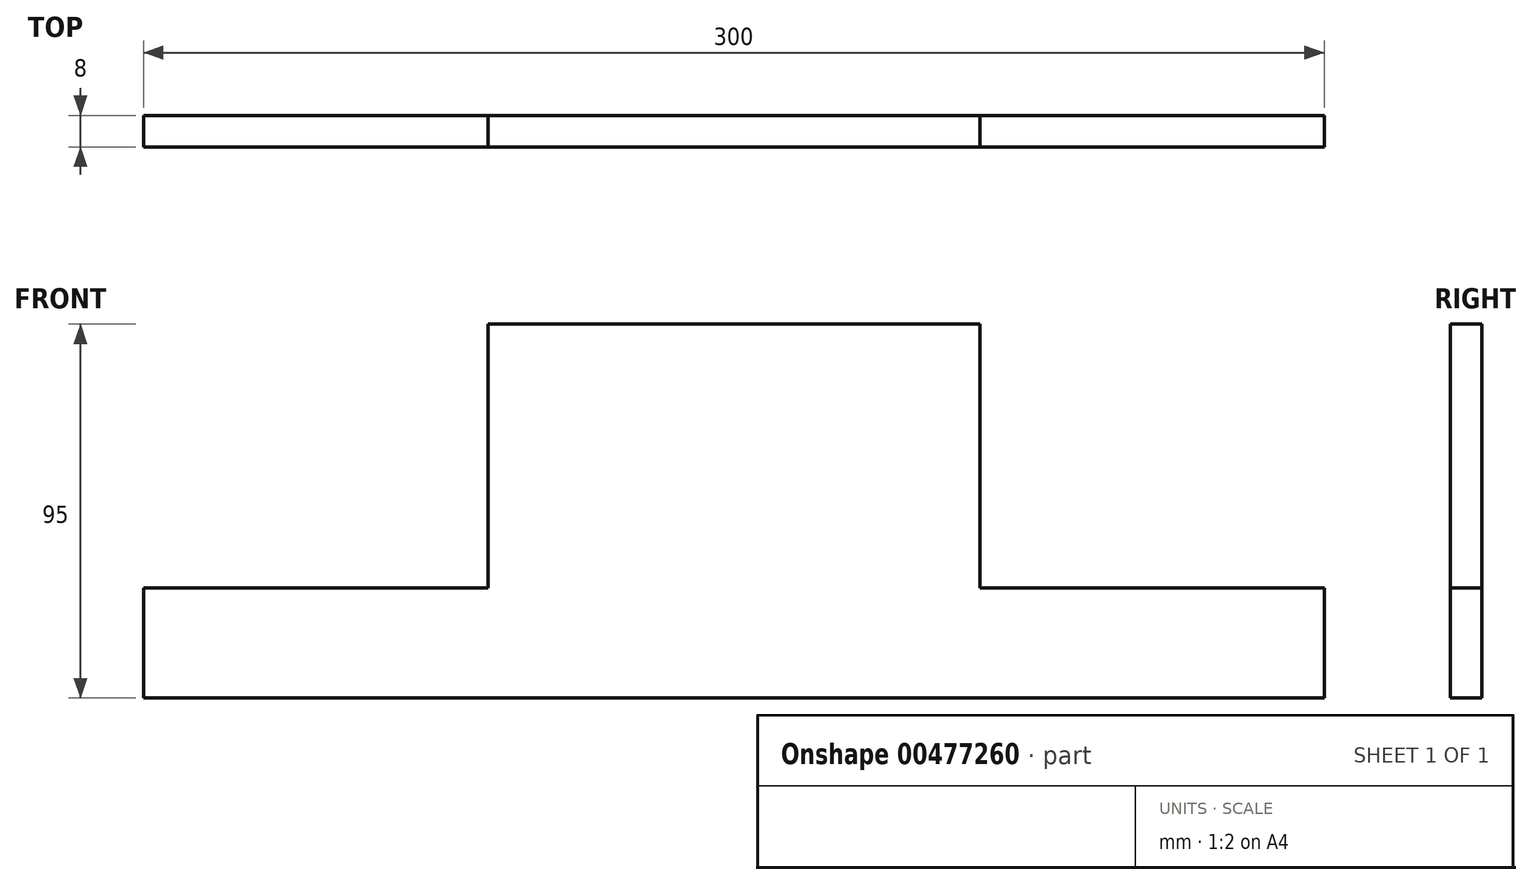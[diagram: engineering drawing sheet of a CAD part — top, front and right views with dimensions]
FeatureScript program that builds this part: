
annotation { "Feature Type Name" : "Feature", "Feature Type Description" : "" }
export const myFeature = defineFeature(function(context is Context, id is Id, definition is map)
    precondition{}
    {
        {
            var Q0;
            Q0=qCreatedBy(makeId("Front.planeOp"),FACE);
            var sketch = newSketch(context, id + "F0", { "sketchPlane" : qUnion([Q0])});
            skLineSegment(sketch, "E0", {"start": v(0, 0) * mm, "end": v(150, 0) * mm});
            skLineSegment(sketch, "E1", {"start": v(150, 0) * mm, "end": v(150, 28) * mm});
            skLineSegment(sketch, "E2", {"start": v(150, 28) * mm, "end": v(62.5, 28) * mm});
            skLineSegment(sketch, "E3", {"start": v(62.5, 28) * mm, "end": v(62.5, 95) * mm});
            skLineSegment(sketch, "E4", {"start": v(62.5, 95) * mm, "end": v(-62.5, 95) * mm});
            skLineSegment(sketch, "E5", {"start": v(-62.5, 95) * mm, "end": v(-62.5, 28) * mm});
            skLineSegment(sketch, "E6", {"start": v(-62.5, 28) * mm, "end": v(-150, 28) * mm});
            skLineSegment(sketch, "E7", {"start": v(-150, 28) * mm, "end": v(-150, 0) * mm});
            skLineSegment(sketch, "E8", {"start": v(-150, 0) * mm, "end": v(0, 0) * mm});
            skSolve(sketch);
        }
        {
            var Q0;
            Q0=makeQuery(id+"F0.imprint","IMPRINT",FACE,{"disambiguationData":[TD([[makeQuery(id+"F0.imprint","IMPRINT",EDGE,{"derivedFrom":sQuery(id+"F0.wireOp",EDGE,"E0")}),1.0]])]});
            extrude(context, id + "F1", {"entities" : qUnion([Q0]), "depth" : 8 * mm});
        }
    });
